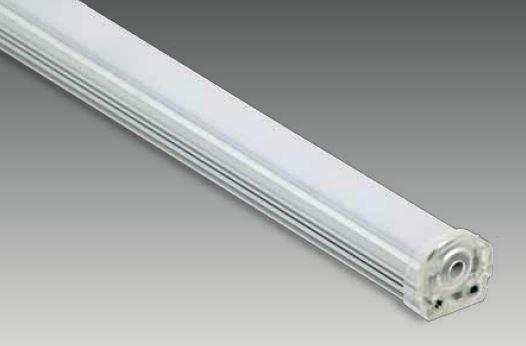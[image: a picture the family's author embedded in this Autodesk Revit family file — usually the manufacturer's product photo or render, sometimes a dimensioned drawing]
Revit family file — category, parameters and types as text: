
# Revit family: SD 0260 CVI
name_source: partatom
category: Lighting Fixtures
revit_build: Autodesk Revit 2017 (Build: 20160225_1515(x64)
units: mm (PartAtom-declared; Revit-internal decimal feet)

## family parameters
Cut with Voids When Loaded = No
Host = Face
Light Source = Yes
Part Type = Normal
Room Calculation Point = No
Round Connector Dimension = Use Diameter
Shared = No

## types (2) — shared parameters
Apparent Load = 4 VA
Color Filter = 16777215
Default Elevation = 1219 mm
Dimming Lamp Color Temperature Shift = <None>
Emit Shape Visible in Rendering = Yes
Emit from Rectangle Length = 15 mm  [stored 0.0492126 ft]
Emit from Rectangle Width = 250 mm  [stored 0.82021 ft]
Light Source Symbol Size = 610 mm
Manufacturer = ARLIGHT
Type Image = SD 0260 CVI.JPG
Wattage Comments = 4

## type names (no varying parameters)
- SDCVI.260.4.30
- SDCVI.260.4.40

note: [stored X ft] marks values corroborated as IEEE doubles in the binary element streams (Revit-internal decimal feet)

## geometry (parser evidence)
native form markers: Sweep x3
no freeform markers — native parametric forms only
